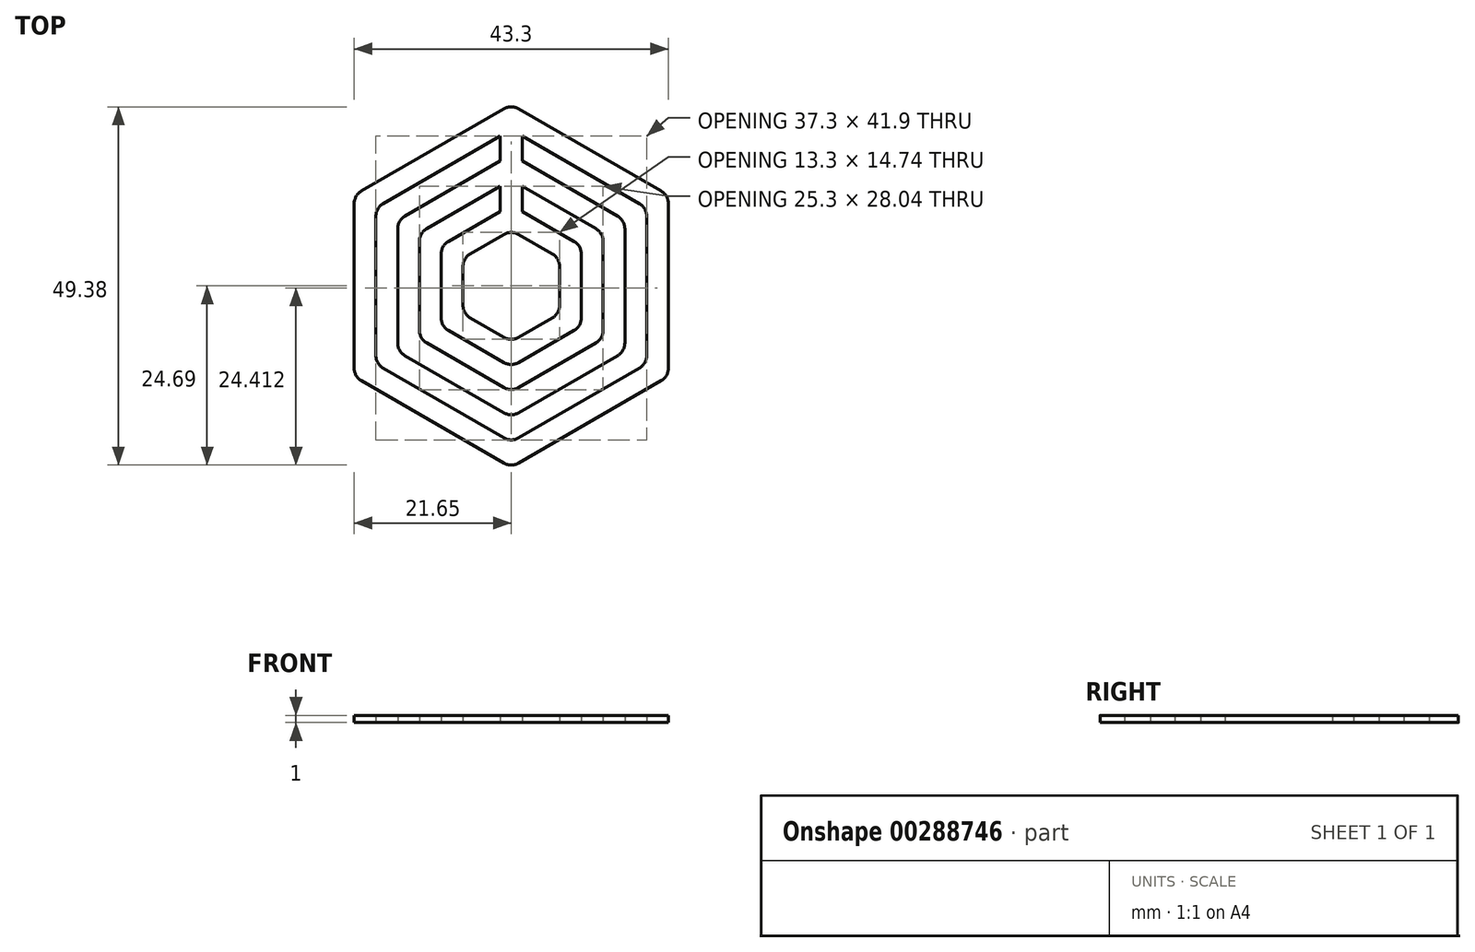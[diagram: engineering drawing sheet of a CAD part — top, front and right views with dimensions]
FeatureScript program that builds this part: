
annotation { "Feature Type Name" : "Feature", "Feature Type Description" : "" }
export const myFeature = defineFeature(function(context is Context, id is Id, definition is map)
    precondition{}
    {
        {
            var Q0;
            Q0=qCreatedBy(makeId("Top.planeOp"),FACE);
            var sketch = newSketch(context, id + "F0", { "sketchPlane" : qUnion([Q0])});
            skCircle(sketch, "E0", {"center": v(0, 0) * mm, "radius": 25 * mm});
            skLineSegment(sketch, "E1", {"start": v(0, 0) * mm, "end": v(0, 8.48) * mm});
            skCircle(sketch, "E2.cCircle", {"center": v(0, 0) * mm, "radius": 25 * mm, "construction": true});
            skLineSegment(sketch, "E2.0", {"start": v(0, 25) * mm, "end": v(21.65, 12.5) * mm});
            skLineSegment(sketch, "E2.1", {"start": v(21.65, 12.5) * mm, "end": v(21.65, -12.5) * mm});
            skLineSegment(sketch, "E2.2", {"start": v(21.65, -12.5) * mm, "end": v(0, -25) * mm});
            skLineSegment(sketch, "E2.3", {"start": v(0, -25) * mm, "end": v(-21.65, -12.5) * mm});
            skLineSegment(sketch, "E2.4", {"start": v(-21.65, -12.5) * mm, "end": v(-21.65, 12.5) * mm});
            skLineSegment(sketch, "E2.5", {"start": v(-21.65, 12.5) * mm, "end": v(0, 25) * mm});
            skLineSegment(sketch, "E3.0", {"start": v(-18.65, -10.77) * mm, "end": v(-18.65, 10.77) * mm});
            skLineSegment(sketch, "E3.1", {"start": v(1.5, 20.67) * mm, "end": v(18.65, 10.77) * mm});
            skLineSegment(sketch, "E3.2", {"start": v(18.65, 10.77) * mm, "end": v(18.65, -10.77) * mm});
            skLineSegment(sketch, "E3.3", {"start": v(-18.65, 10.77) * mm, "end": v(-1.5, 20.67) * mm});
            skLineSegment(sketch, "E3.4", {"start": v(18.65, -10.77) * mm, "end": v(0, -21.54) * mm});
            skLineSegment(sketch, "E3.5", {"start": v(0, -21.54) * mm, "end": v(-18.65, -10.77) * mm});
            skLineSegment(sketch, "E4.0", {"start": v(-15.65, -9.04) * mm, "end": v(-15.65, 9.04) * mm});
            skLineSegment(sketch, "E4.1", {"start": v(1.5, 17.2) * mm, "end": v(15.65, 9.04) * mm});
            skLineSegment(sketch, "E4.2", {"start": v(15.65, 9.04) * mm, "end": v(15.65, -9.04) * mm});
            skLineSegment(sketch, "E4.3", {"start": v(-15.65, 9.04) * mm, "end": v(-1.5, 17.2) * mm});
            skLineSegment(sketch, "E4.4", {"start": v(15.65, -9.04) * mm, "end": v(0, -18.07) * mm});
            skLineSegment(sketch, "E4.5", {"start": v(0, -18.07) * mm, "end": v(-15.65, -9.04) * mm});
            skLineSegment(sketch, "E5.0", {"start": v(-12.65, -7.3) * mm, "end": v(-12.65, 7.3) * mm});
            skLineSegment(sketch, "E5.1", {"start": v(1.5, 13.74) * mm, "end": v(12.65, 7.3) * mm});
            skLineSegment(sketch, "E5.2", {"start": v(12.65, 7.3) * mm, "end": v(12.65, -7.3) * mm});
            skLineSegment(sketch, "E5.3", {"start": v(-12.65, 7.3) * mm, "end": v(-1.5, 13.74) * mm});
            skLineSegment(sketch, "E5.4", {"start": v(12.65, -7.3) * mm, "end": v(0, -14.6) * mm});
            skLineSegment(sketch, "E5.5", {"start": v(0, -14.6) * mm, "end": v(-12.65, -7.3) * mm});
            skLineSegment(sketch, "E6.0", {"start": v(-9.65, -5.57) * mm, "end": v(-9.65, 5.57) * mm});
            skLineSegment(sketch, "E6.1", {"start": v(1.5, 10.28) * mm, "end": v(9.65, 5.57) * mm});
            skLineSegment(sketch, "E6.2", {"start": v(9.65, 5.57) * mm, "end": v(9.65, -5.57) * mm});
            skLineSegment(sketch, "E6.3", {"start": v(-9.65, 5.57) * mm, "end": v(-1.5, 10.28) * mm});
            skLineSegment(sketch, "E6.4", {"start": v(9.65, -5.57) * mm, "end": v(0, -11.14) * mm});
            skLineSegment(sketch, "E6.5", {"start": v(0, -11.14) * mm, "end": v(-9.65, -5.57) * mm});
            skLineSegment(sketch, "E7.0", {"start": v(-6.65, -3.84) * mm, "end": v(-6.65, 3.84) * mm});
            skLineSegment(sketch, "E7.1", {"start": v(1.5, 6.81) * mm, "end": v(6.65, 3.84) * mm});
            skLineSegment(sketch, "E7.2", {"start": v(6.65, 3.84) * mm, "end": v(6.65, -3.84) * mm});
            skLineSegment(sketch, "E7.3", {"start": v(-6.65, 3.84) * mm, "end": v(-1.5, 6.81) * mm});
            skLineSegment(sketch, "E7.4", {"start": v(6.65, -3.84) * mm, "end": v(0, -7.68) * mm});
            skLineSegment(sketch, "E7.5", {"start": v(0, -7.68) * mm, "end": v(-6.65, -3.84) * mm});
            skLineSegment(sketch, "E8", {"start": v(0, 25) * mm, "end": v(-1.5, 25) * mm});
            skLineSegment(sketch, "E9", {"start": v(-1.5, 25) * mm, "end": v(-1.5, 24.13) * mm});
            skPoint(sketch, "E9.endSnap0", {"position": v(-18.65, 0) * mm});
            skLineSegment(sketch, "E10", {"start": v(0, 25) * mm, "end": v(1.5, 25) * mm});
            skLineSegment(sketch, "E11", {"start": v(1.5, 25) * mm, "end": v(1.5, 24.13) * mm});
            skLineSegment(sketch, "E12.trimOffspring", {"start": v(-1.5, 20.67) * mm, "end": v(-1.5, 17.2) * mm});
            skLineSegment(sketch, "E13.trimOffspring", {"start": v(1.5, 20.67) * mm, "end": v(1.5, 17.2) * mm});
            skLineSegment(sketch, "E14.trimOffspring", {"start": v(-1.5, 13.74) * mm, "end": v(-1.5, 10.28) * mm});
            skLineSegment(sketch, "E15.trimOffspring", {"start": v(1.5, 13.74) * mm, "end": v(1.5, 10.28) * mm});
            skPoint(sketch, "E16.start.orphan", {"position": v(-1.5, 0) * mm});
            skPoint(sketch, "E17.start.orphan", {"position": v(1.5, 0) * mm});
            skLineSegment(sketch, "E18", {"start": v(1.5, 6.81) * mm, "end": v(0, 7.68) * mm});
            skLineSegment(sketch, "E19.trimOffspring", {"start": v(9, 12.88) * mm, "end": v(9.31, 13.06) * mm});
            skLineSegment(sketch, "E20", {"start": v(0, 7.68) * mm, "end": v(-1.5, 6.81) * mm});
            skSolve(sketch);
        }
        {
            var Q0;
            {var subQ0=sQuery(id+"F0.wireOp",EDGE,"E2.1");Q0=makeQuery(id+"F0.imprint","IMPRINT",FACE,{"disambiguationData":[TD([[makeQuery(id+"F0.imprint","IMPRINT",EDGE,{"derivedFrom":subQ0}),-1.0]])]});}
            extrude(context, id + "F1", {"entities" : qUnion([Q0]), "depth" : 1 * mm});
        }
        {
            var Q0;
            Q0=makeQuery(id+"F1.opExtrude","SWEPT_EDGE",EDGE,{"disambiguationData":[OSD([sQuery(id+"F0.wireOp",EDGE,"E0"),sQuery(id+"F0.wireOp",EDGE,"E2.0"),sQuery(id+"F0.wireOp",EDGE,"E2.5"),sQuery(id+"F0.wireOp",EDGE,"E8"),sQuery(id+"F0.wireOp",EDGE,"E10")])]});
            var Q1;
            Q1=makeQuery(id+"F1.opExtrude","SWEPT_EDGE",EDGE,{"disambiguationData":[OSD([sQuery(id+"F0.wireOp",EDGE,"E0"),sQuery(id+"F0.wireOp",EDGE,"E2.4"),sQuery(id+"F0.wireOp",EDGE,"E2.5")])]});
            var Q2;
            Q2=makeQuery(id+"F1.opExtrude","SWEPT_EDGE",EDGE,{"disambiguationData":[OSD([sQuery(id+"F0.wireOp",EDGE,"E0"),sQuery(id+"F0.wireOp",EDGE,"E2.3"),sQuery(id+"F0.wireOp",EDGE,"E2.4")])]});
            var Q3;
            Q3=makeQuery(id+"F1.opExtrude","SWEPT_EDGE",EDGE,{"disambiguationData":[OSD([sQuery(id+"F0.wireOp",EDGE,"E0"),sQuery(id+"F0.wireOp",EDGE,"E2.0"),sQuery(id+"F0.wireOp",EDGE,"E2.1")])]});
            var Q4;
            Q4=makeQuery(id+"F1.opExtrude","SWEPT_EDGE",EDGE,{"disambiguationData":[OSD([sQuery(id+"F0.wireOp",EDGE,"E0"),sQuery(id+"F0.wireOp",EDGE,"E2.1"),sQuery(id+"F0.wireOp",EDGE,"E2.2")])]});
            var Q5;
            Q5=makeQuery(id+"F1.opExtrude","SWEPT_EDGE",EDGE,{"disambiguationData":[OSD([sQuery(id+"F0.wireOp",EDGE,"E0"),sQuery(id+"F0.wireOp",EDGE,"E2.2"),sQuery(id+"F0.wireOp",EDGE,"E2.3")])]});
            var Q6;
            Q6=makeQuery(id+"F1.opExtrude","SWEPT_EDGE",EDGE,{"disambiguationData":[OSD([sQuery(id+"F0.wireOp",EDGE,"E3.0"),sQuery(id+"F0.wireOp",EDGE,"E3.5")])]});
            var Q7;
            Q7=makeQuery(id+"F1.opExtrude","SWEPT_EDGE",EDGE,{"disambiguationData":[OSD([sQuery(id+"F0.wireOp",EDGE,"E3.0"),sQuery(id+"F0.wireOp",EDGE,"E3.3")])]});
            var Q8;
            Q8=makeQuery(id+"F1.opExtrude","SWEPT_EDGE",EDGE,{"disambiguationData":[OSD([sQuery(id+"F0.wireOp",EDGE,"E3.1"),sQuery(id+"F0.wireOp",EDGE,"E3.2")])]});
            var Q9;
            Q9=makeQuery(id+"F1.opExtrude","SWEPT_EDGE",EDGE,{"disambiguationData":[OSD([sQuery(id+"F0.wireOp",EDGE,"E3.2"),sQuery(id+"F0.wireOp",EDGE,"E3.4")])]});
            var Q10;
            Q10=makeQuery(id+"F1.opExtrude","SWEPT_EDGE",EDGE,{"disambiguationData":[OSD([sQuery(id+"F0.wireOp",EDGE,"E3.4"),sQuery(id+"F0.wireOp",EDGE,"E3.5")])]});
            var Q11;
            Q11=makeQuery(id+"F1.opExtrude","SWEPT_EDGE",EDGE,{"disambiguationData":[OSD([sQuery(id+"F0.wireOp",EDGE,"E5.4"),sQuery(id+"F0.wireOp",EDGE,"E5.5")])]});
            var Q12;
            Q12=makeQuery(id+"F1.opExtrude","SWEPT_EDGE",EDGE,{"disambiguationData":[OSD([sQuery(id+"F0.wireOp",EDGE,"E4.0"),sQuery(id+"F0.wireOp",EDGE,"E4.5")])]});
            var Q13;
            Q13=makeQuery(id+"F1.opExtrude","SWEPT_EDGE",EDGE,{"disambiguationData":[OSD([sQuery(id+"F0.wireOp",EDGE,"E4.0"),sQuery(id+"F0.wireOp",EDGE,"E4.3")])]});
            var Q14;
            Q14=makeQuery(id+"F1.opExtrude","SWEPT_EDGE",EDGE,{"disambiguationData":[OSD([sQuery(id+"F0.wireOp",EDGE,"E6.0"),sQuery(id+"F0.wireOp",EDGE,"E6.3")])]});
            var Q15;
            Q15=makeQuery(id+"F1.opExtrude","SWEPT_EDGE",EDGE,{"disambiguationData":[OSD([sQuery(id+"F0.wireOp",EDGE,"E6.0"),sQuery(id+"F0.wireOp",EDGE,"E6.5")])]});
            var Q16;
            Q16=makeQuery(id+"F1.opExtrude","SWEPT_EDGE",EDGE,{"disambiguationData":[OSD([sQuery(id+"F0.wireOp",EDGE,"E6.4"),sQuery(id+"F0.wireOp",EDGE,"E6.5")])]});
            var Q17;
            Q17=makeQuery(id+"F1.opExtrude","SWEPT_EDGE",EDGE,{"disambiguationData":[OSD([sQuery(id+"F0.wireOp",EDGE,"E6.2"),sQuery(id+"F0.wireOp",EDGE,"E6.4")])]});
            var Q18;
            Q18=makeQuery(id+"F1.opExtrude","SWEPT_EDGE",EDGE,{"disambiguationData":[OSD([sQuery(id+"F0.wireOp",EDGE,"E6.1"),sQuery(id+"F0.wireOp",EDGE,"E6.2")])]});
            var Q19;
            Q19=makeQuery(id+"F1.opExtrude","SWEPT_EDGE",EDGE,{"disambiguationData":[OSD([sQuery(id+"F0.wireOp",EDGE,"E5.1"),sQuery(id+"F0.wireOp",EDGE,"E5.2")])]});
            var Q20;
            Q20=makeQuery(id+"F1.opExtrude","SWEPT_EDGE",EDGE,{"disambiguationData":[OSD([sQuery(id+"F0.wireOp",EDGE,"E5.0"),sQuery(id+"F0.wireOp",EDGE,"E5.5")])]});
            var Q21;
            Q21=makeQuery(id+"F1.opExtrude","SWEPT_EDGE",EDGE,{"disambiguationData":[OSD([sQuery(id+"F0.wireOp",EDGE,"E7.0"),sQuery(id+"F0.wireOp",EDGE,"E7.3")])]});
            var Q22;
            Q22=makeQuery(id+"F1.opExtrude","SWEPT_EDGE",EDGE,{"disambiguationData":[OSD([sQuery(id+"F0.wireOp",EDGE,"E7.0"),sQuery(id+"F0.wireOp",EDGE,"E7.5")])]});
            var Q23;
            Q23=makeQuery(id+"F1.opExtrude","SWEPT_EDGE",EDGE,{"disambiguationData":[OSD([sQuery(id+"F0.wireOp",EDGE,"E5.0"),sQuery(id+"F0.wireOp",EDGE,"E5.3")])]});
            var Q24;
            Q24=makeQuery(id+"F1.opExtrude","SWEPT_EDGE",EDGE,{"disambiguationData":[OSD([sQuery(id+"F0.wireOp",EDGE,"E18"),sQuery(id+"F0.wireOp",EDGE,"E20")])]});
            var Q25;
            Q25=makeQuery(id+"F1.opExtrude","SWEPT_EDGE",EDGE,{"disambiguationData":[OSD([sQuery(id+"F0.wireOp",EDGE,"E7.1"),sQuery(id+"F0.wireOp",EDGE,"E7.2")])]});
            var Q26;
            Q26=makeQuery(id+"F1.opExtrude","SWEPT_EDGE",EDGE,{"disambiguationData":[OSD([sQuery(id+"F0.wireOp",EDGE,"E7.2"),sQuery(id+"F0.wireOp",EDGE,"E7.4")])]});
            var Q27;
            Q27=makeQuery(id+"F1.opExtrude","SWEPT_EDGE",EDGE,{"disambiguationData":[OSD([sQuery(id+"F0.wireOp",EDGE,"E7.4"),sQuery(id+"F0.wireOp",EDGE,"E7.5")])]});
            var Q28;
            Q28=makeQuery(id+"F1.opExtrude","SWEPT_EDGE",EDGE,{"disambiguationData":[OSD([sQuery(id+"F0.wireOp",EDGE,"E5.2"),sQuery(id+"F0.wireOp",EDGE,"E5.4")])]});
            var Q29;
            Q29=makeQuery(id+"F1.opExtrude","SWEPT_EDGE",EDGE,{"disambiguationData":[OSD([sQuery(id+"F0.wireOp",EDGE,"E4.2"),sQuery(id+"F0.wireOp",EDGE,"E4.4")])]});
            var Q30;
            Q30=makeQuery(id+"F1.opExtrude","SWEPT_EDGE",EDGE,{"disambiguationData":[OSD([sQuery(id+"F0.wireOp",EDGE,"E4.4"),sQuery(id+"F0.wireOp",EDGE,"E4.5")])]});
            var Q31;
            Q31=makeQuery(id+"F1.opExtrude","SWEPT_EDGE",EDGE,{"disambiguationData":[OSD([sQuery(id+"F0.wireOp",EDGE,"E4.1"),sQuery(id+"F0.wireOp",EDGE,"E4.2")])]});
            fillet(context, id + "F2", {"entities" : qUnion([Q0, Q1, Q2, Q3, Q4, Q5, Q6, Q7, Q8, Q9, Q10, Q11, Q12, Q13, Q14, Q15, Q16, Q17, Q18, Q19, Q20, Q21, Q22, Q23, Q24, Q25, Q26, Q27, Q28, Q29, Q30, Q31]), "radius" : 2 * mm, "tangentPropagation" : true, "allowEdgeOverflow" : false});
        }
    });
